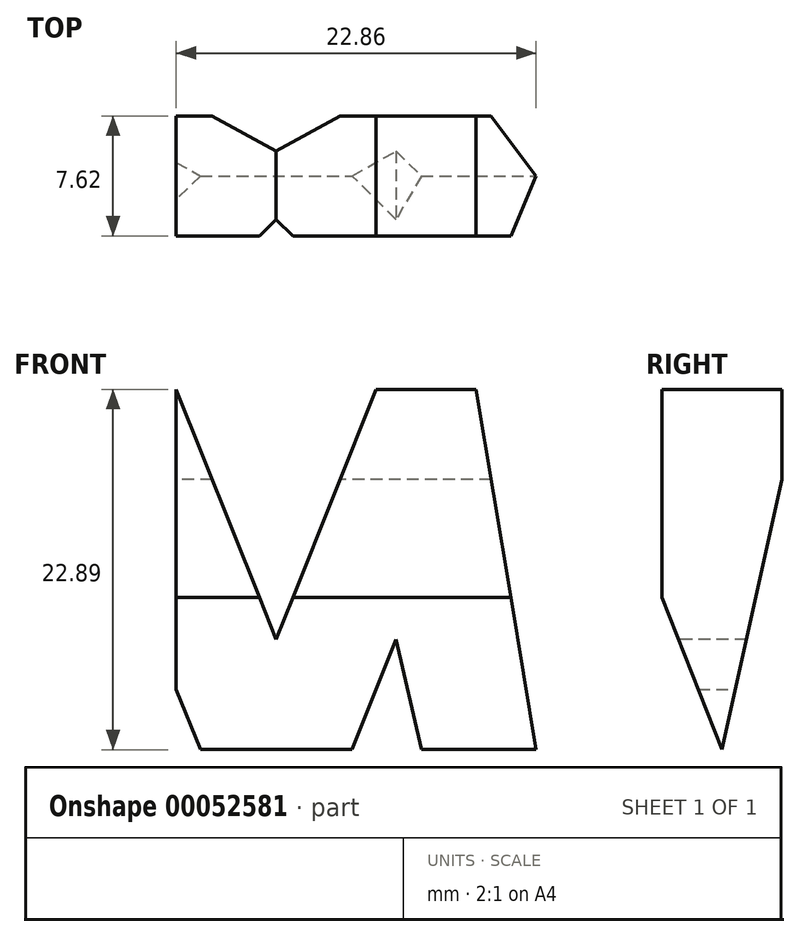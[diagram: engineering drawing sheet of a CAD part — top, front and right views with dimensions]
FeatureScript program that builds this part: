
annotation { "Feature Type Name" : "Feature", "Feature Type Description" : "" }
export const myFeature = defineFeature(function(context is Context, id is Id, definition is map)
    precondition{}
    {
        {
            var Q0;
            Q0=qCreatedBy(makeId("Front.planeOp"),FACE);
            var sketch = newSketch(context, id + "F0", { "sketchPlane" : qUnion([Q0])});
            skLineSegment(sketch, "E0", {"start": v(0, 0) * mm, "end": v(-38.1, 0) * mm});
            skLineSegment(sketch, "E1", {"start": v(-38.1, 0) * mm, "end": v(-38.1, 38.1) * mm});
            skLineSegment(sketch, "E2", {"start": v(-38.1, 38.1) * mm, "end": v(0, 38.1) * mm});
            skLineSegment(sketch, "E3", {"start": v(0, 38.1) * mm, "end": v(0, 0) * mm});
            skSolve(sketch);
        }
        {
            var Q0;
            Q0 = qSketchRegion(id + "F0", true);
            var Q1;
            Q1=makeQuery(id+"F0.imprint","IMPRINT",FACE,{"disambiguationData":[TD([[makeQuery(id+"F0.imprint","IMPRINT",EDGE,{"derivedFrom":sQuery(id+"F0.wireOp",EDGE,"E0")}),-1.0]])]});
            extrude(context, id + "F1", {"entities" : qUnion([Q0, Q1]), "depth" : 38.1 * mm});
        }
        {
            var Q0;
            Q0=qCreatedBy(makeId("Front.planeOp"),FACE);
            cPlane(context, id + "F2", {"entities" : qUnion([Q0]), "cplaneType" : CPlaneType.OFFSET, "offset" : 38.1 * mm, "width" : 152.4 * mm, "height" : 152.4 * mm});
        }
        {
            var Q0;
            Q0=qCreatedBy(makeId("Right.planeOp"),FACE);
            cPlane(context, id + "F3", {"entities" : qUnion([Q0]), "cplaneType" : CPlaneType.OFFSET, "offset" : 38.1 * mm, "width" : 152.4 * mm, "height" : 152.4 * mm});
        }
        {
            var Q0;
            Q0=qCreatedBy(makeId("Top.planeOp"),FACE);
            cPlane(context, id + "F4", {"entities" : qUnion([Q0]), "cplaneType" : CPlaneType.OFFSET, "offset" : 38.1 * mm, "width" : 152.4 * mm, "height" : 152.4 * mm});
        }
        {
            var Q0;
            Q0=qCreatedBy(id+"F3.planeOp",FACE);
            var sketch = newSketch(context, id + "F5", { "sketchPlane" : qUnion([Q0])});
            skLineSegment(sketch, "E4", {"start": v(0, 0) * mm, "end": v(0, 38.1) * mm});
            skLineSegment(sketch, "E5", {"start": v(0, 38.1) * mm, "end": v(-38.1, 38.1) * mm});
            skLineSegment(sketch, "E6", {"start": v(-38.1, 38.1) * mm, "end": v(-38.1, 0) * mm});
            skLineSegment(sketch, "E7", {"start": v(-38.1, 0) * mm, "end": v(0, 0) * mm});
            skLineSegment(sketch, "E8", {"start": v(-38.1, 38.1) * mm, "end": v(-31.75, 38.1) * mm});
            skLineSegment(sketch, "E9", {"start": v(-31.75, 38.1) * mm, "end": v(-26.67, 15.39) * mm});
            skLineSegment(sketch, "E10", {"start": v(-26.67, 15.39) * mm, "end": v(-21.59, 28.09) * mm});
            skLineSegment(sketch, "E11", {"start": v(-21.59, 28.09) * mm, "end": v(-16.5, 28.09) * mm});
            skLineSegment(sketch, "E12", {"start": v(-16.5, 28.09) * mm, "end": v(-11.43, 15.21) * mm});
            skLineSegment(sketch, "E13", {"start": v(-11.43, 15.21) * mm, "end": v(-6.35, 38.1) * mm});
            skLineSegment(sketch, "E14", {"start": v(-6.35, 38.1) * mm, "end": v(0, 38.1) * mm});
            skLineSegment(sketch, "E15", {"start": v(0, 38.1) * mm, "end": v(-6.35, 0) * mm});
            skLineSegment(sketch, "E16", {"start": v(-6.35, 0) * mm, "end": v(-12.7, 0) * mm});
            skLineSegment(sketch, "E17", {"start": v(-12.7, 0) * mm, "end": v(-19.05, 15.88) * mm});
            skLineSegment(sketch, "E18", {"start": v(-19.05, 15.88) * mm, "end": v(-25.4, 0) * mm});
            skLineSegment(sketch, "E19", {"start": v(-25.4, 0) * mm, "end": v(-31.75, 0) * mm});
            skLineSegment(sketch, "E20", {"start": v(-31.75, 0) * mm, "end": v(-38.1, 38.1) * mm});
            skSolve(sketch);
        }
        {
            var Q0;
            Q0=makeQuery(id+"F5.imprint","IMPRINT",FACE,{"disambiguationData":[TD([[makeQuery(id+"F5.imprint","IMPRINT",EDGE,{"derivedFrom":sQuery(id+"F5.wireOp",EDGE,"E5")}),1.0]])]});
            var Q1;
            {var subQ0=sQuery(id+"F5.wireOp",EDGE,"E6");Q1=makeQuery(id+"F5.imprint","IMPRINT",FACE,{"disambiguationData":[TD([[makeQuery(id+"F5.imprint","IMPRINT",EDGE,{"derivedFrom":subQ0}),1.0]])]});}
            var Q2;
            {var subQ0=sQuery(id+"F5.wireOp",EDGE,"E17");Q2=makeQuery(id+"F5.imprint","IMPRINT",FACE,{"disambiguationData":[TD([[makeQuery(id+"F5.imprint","IMPRINT",EDGE,{"derivedFrom":subQ0}),1.0]])]});}
            var Q3;
            {var subQ0=sQuery(id+"F5.wireOp",EDGE,"E4");Q3=makeQuery(id+"F5.imprint","IMPRINT",FACE,{"disambiguationData":[TD([[makeQuery(id+"F5.imprint","IMPRINT",EDGE,{"derivedFrom":subQ0}),1.0]])]});}
            extrude(context, id + "F6", {"entities" : qUnion([Q0, Q1, Q2, Q3]), "operationType" : NewBodyOperationType.REMOVE, "oppositeDirection" : true, "depth" : 76.2 * mm});
        }
        {
            var Q0;
            Q0=qCreatedBy(id+"F2.planeOp",FACE);
            var sketch = newSketch(context, id + "F7", { "sketchPlane" : qUnion([Q0])});
            skLineSegment(sketch, "E21", {"start": v(0, 0) * mm, "end": v(0, 38.1) * mm});
            skLineSegment(sketch, "E22", {"start": v(0, 38.1) * mm, "end": v(-38.1, 38.1) * mm});
            skLineSegment(sketch, "E23", {"start": v(-38.1, 38.1) * mm, "end": v(-38.1, 0) * mm});
            skLineSegment(sketch, "E24", {"start": v(-38.1, 0) * mm, "end": v(0, 0) * mm});
            skLineSegment(sketch, "E25", {"start": v(-38.1, 0) * mm, "end": v(-31.75, 38.1) * mm});
            skLineSegment(sketch, "E26", {"start": v(-31.75, 38.1) * mm, "end": v(-25.4, 38.1) * mm});
            skLineSegment(sketch, "E27", {"start": v(-25.4, 38.1) * mm, "end": v(-19.05, 22.23) * mm});
            skLineSegment(sketch, "E28", {"start": v(-19.05, 22.23) * mm, "end": v(-12.7, 38.1) * mm});
            skLineSegment(sketch, "E29", {"start": v(-12.7, 38.1) * mm, "end": v(-6.35, 38.1) * mm});
            skLineSegment(sketch, "E30", {"start": v(-6.35, 38.1) * mm, "end": v(0, 0) * mm});
            skLineSegment(sketch, "E31", {"start": v(-6.35, 0) * mm, "end": v(-11.43, 22.22) * mm});
            skLineSegment(sketch, "E32", {"start": v(-11.43, 22.22) * mm, "end": v(-16.5, 9.53) * mm});
            skLineSegment(sketch, "E33", {"start": v(-16.5, 9.53) * mm, "end": v(-21.59, 9.53) * mm});
            skLineSegment(sketch, "E34", {"start": v(-21.59, 9.52) * mm, "end": v(-26.67, 22.23) * mm});
            skLineSegment(sketch, "E35", {"start": v(-26.67, 22.23) * mm, "end": v(-31.75, 0) * mm});
            skLineSegment(sketch, "E36", {"start": v(-31.75, 0) * mm, "end": v(-38.1, 0) * mm});
            skSolve(sketch);
        }
        {
            var Q0;
            {var subQ0=sQuery(id+"F7.wireOp",EDGE,"E27");Q0=makeQuery(id+"F7.imprint","IMPRINT",FACE,{"disambiguationData":[TD([[makeQuery(id+"F7.imprint","IMPRINT",EDGE,{"derivedFrom":subQ0}),1.0]])]});}
            var Q1;
            {var subQ0=sQuery(id+"F7.wireOp",EDGE,"E23");Q1=makeQuery(id+"F7.imprint","IMPRINT",FACE,{"disambiguationData":[TD([[makeQuery(id+"F7.imprint","IMPRINT",EDGE,{"derivedFrom":subQ0}),1.0]])]});}
            var Q2;
            {var subQ0=sQuery(id+"F7.wireOp",EDGE,"E31");Q2=makeQuery(id+"F7.imprint","IMPRINT",FACE,{"disambiguationData":[TD([[makeQuery(id+"F7.imprint","IMPRINT",EDGE,{"derivedFrom":subQ0}),1.0]])]});}
            var Q3;
            {var subQ0=sQuery(id+"F7.wireOp",EDGE,"E21");Q3=makeQuery(id+"F7.imprint","IMPRINT",FACE,{"disambiguationData":[TD([[makeQuery(id+"F7.imprint","IMPRINT",EDGE,{"derivedFrom":subQ0}),1.0]])]});}
            extrude(context, id + "F8", {"entities" : qUnion([Q0, Q1, Q2, Q3]), "operationType" : NewBodyOperationType.REMOVE, "oppositeDirection" : true, "depth" : 76.2 * mm});
        }
        {
            var Q0;
            Q0=qCreatedBy(id+"F4.planeOp",FACE);
            var sketch = newSketch(context, id + "F9", { "sketchPlane" : qUnion([Q0])});
            skLineSegment(sketch, "E37", {"start": v(0, 0) * mm, "end": v(-38.1, 0) * mm});
            skLineSegment(sketch, "E38", {"start": v(-38.1, 0) * mm, "end": v(-38.1, -38.1) * mm});
            skLineSegment(sketch, "E39", {"start": v(-38.1, -38.1) * mm, "end": v(0, -38.1) * mm});
            skLineSegment(sketch, "E40", {"start": v(0, -38.1) * mm, "end": v(0, 0) * mm});
            skLineSegment(sketch, "E41", {"start": v(-38.1, -22.86) * mm, "end": v(-12.7, -22.86) * mm});
            skLineSegment(sketch, "E42", {"start": v(-12.7, -22.86) * mm, "end": v(-12.7, -30.48) * mm});
            skLineSegment(sketch, "E43", {"start": v(-12.7, -30.48) * mm, "end": v(-38.1, -30.48) * mm});
            skLineSegment(sketch, "E44", {"start": v(-38.1, -30.48) * mm, "end": v(-38.1, -38.1) * mm});
            skLineSegment(sketch, "E45", {"start": v(0, -38.1) * mm, "end": v(0, -15.24) * mm});
            skLineSegment(sketch, "E46", {"start": v(0, -15.24) * mm, "end": v(-25.4, -15.24) * mm});
            skLineSegment(sketch, "E47", {"start": v(-25.4, -15.24) * mm, "end": v(-25.4, -7.62) * mm});
            skLineSegment(sketch, "E48", {"start": v(-25.4, -7.62) * mm, "end": v(0, -7.62) * mm});
            skLineSegment(sketch, "E49", {"start": v(0, -7.62) * mm, "end": v(0, 0) * mm});
            skSolve(sketch);
        }
        {
            var Q0;
            {var subQ2=sQuery(id+"F9.wireOp",EDGE,"E41");Q0=makeQuery(id+"F9.imprint","IMPRINT",FACE,{"disambiguationData":[TD([[makeQuery(id+"F9.imprint","IMPRINT",EDGE,{"derivedFrom":subQ2}),-1.0]])]});}
            var Q1;
            Q1=makeQuery(id+"F9.imprint","IMPRINT",FACE,{"disambiguationData":[TD([[makeQuery(id+"F9.imprint","IMPRINT",EDGE,{"derivedFrom":sQuery(id+"F9.wireOp",EDGE,"E40")}),1.0]])]});
            extrude(context, id + "F10", {"entities" : qUnion([Q0, Q1]), "operationType" : NewBodyOperationType.REMOVE, "oppositeDirection" : true, "depth" : 76.2 * mm});
        }
    });
